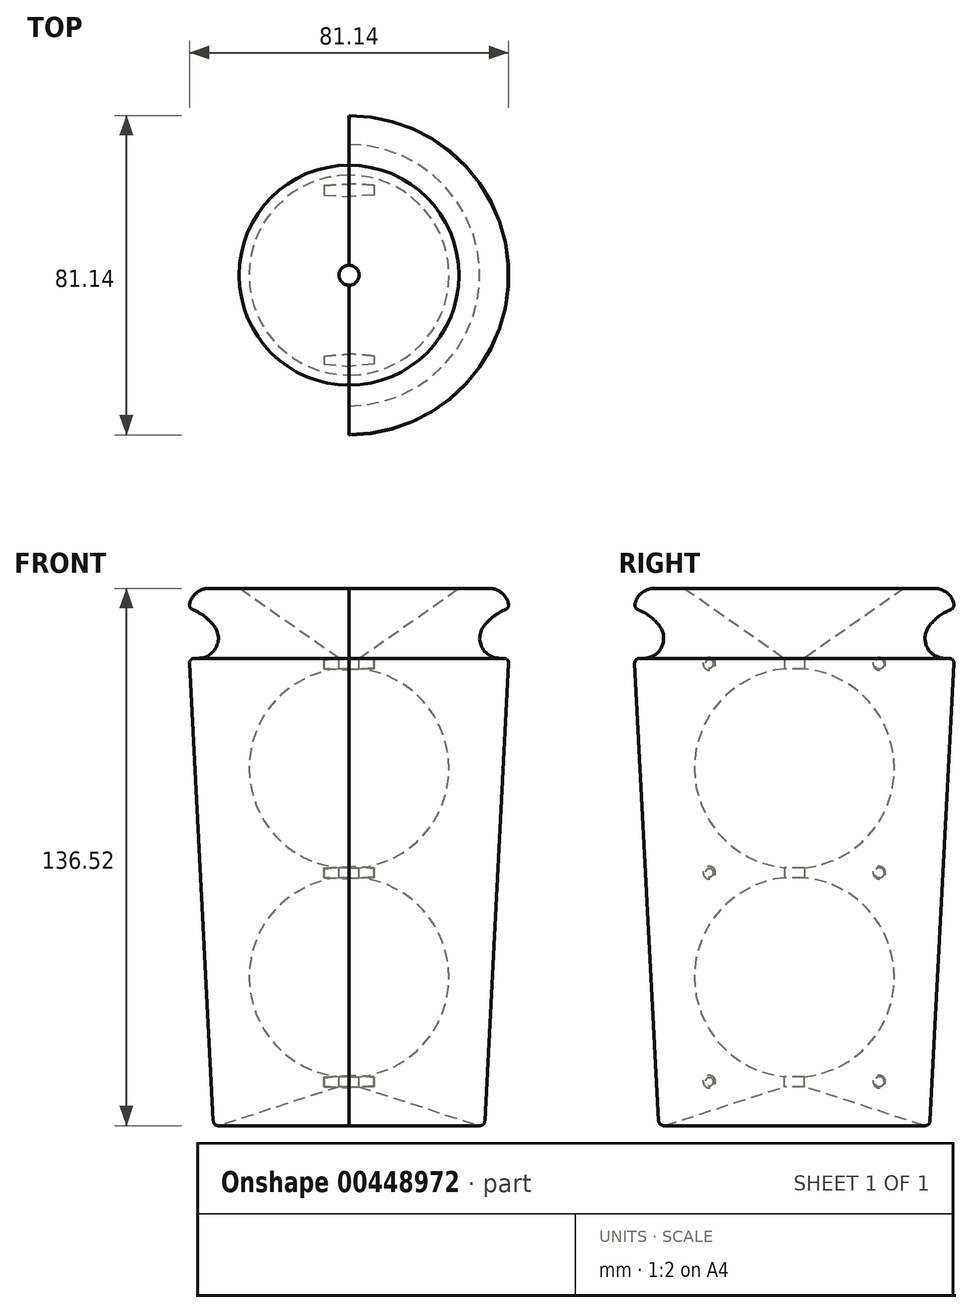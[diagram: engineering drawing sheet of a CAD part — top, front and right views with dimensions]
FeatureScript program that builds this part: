
annotation { "Feature Type Name" : "Feature", "Feature Type Description" : "" }
export const myFeature = defineFeature(function(context is Context, id is Id, definition is map)
    precondition{}
    {
        {
            var Q0;
            Q0=qCreatedBy(makeId("Front.planeOp"),FACE);
            var sketch = newSketch(context, id + "F0", { "sketchPlane" : qUnion([Q0])});
            skLineSegment(sketch, "E0", {"start": v(-40.64, 0) * mm, "end": v(-34.4, -119.19) * mm});
            skLineSegment(sketch, "E1", {"start": v(-40.64, 0) * mm, "end": v(-31.74, 0) * mm});
            skArc(sketch, "E2", {"start": v(-2.54, -2.67) * mm, "mid": v(-25.4, -27.94) * mm, "end": v(-2.54, -53.21) * mm});
            skLineSegment(sketch, "E3", {"start": v(-40.63, 17.78) * mm, "end": v(-27.93, 17.78) * mm});
            skLineSegment(sketch, "E4", {"start": v(-27.93, 17.78) * mm, "end": v(-2.54, 0) * mm});
            skLineSegment(sketch, "E5", {"start": v(-2.54, 0) * mm, "end": v(-2.54, -2.67) * mm});
            skPoint(sketch, "E6", {"position": v(-20.32, 0) * mm});
            skLineSegment(sketch, "E7", {"start": v(-40.63, 17.78) * mm, "end": v(-40.63, 12.7) * mm});
            skArc(sketch, "E8", {"start": v(-31.74, 0) * mm, "mid": v(-34.02, 7.86) * mm, "end": v(-40.63, 12.7) * mm});
            skPoint(sketch, "E9.end.orphan", {"position": v(0, -2.54) * mm});
            skPoint(sketch, "E9.start.orphan", {"position": v(0, 0) * mm});
            skLineSegment(sketch, "E10", {"start": v(-2.54, -53.21) * mm, "end": v(-2.54, -55.75) * mm});
            skArc(sketch, "E11", {"start": v(-2.54, -55.75) * mm, "mid": v(-25.4, -81.03) * mm, "end": v(-2.54, -106.3) * mm});
            skLineSegment(sketch, "E12", {"start": v(-2.54, -108.84) * mm, "end": v(-2.54, -106.3) * mm});
            skLineSegment(sketch, "E13", {"start": v(-2.54, -106.3) * mm, "end": v(-2.54, -55.75) * mm, "construction": true});
            skLineSegment(sketch, "E14", {"start": v(-2.54, -53.21) * mm, "end": v(-2.54, -2.67) * mm, "construction": true});
            skPoint(sketch, "E15.orphan", {"position": v(0, -108.84) * mm});
            skPoint(sketch, "E16.trimOffspring.start.orphan", {"position": v(0, -53.34) * mm});
            skLineSegment(sketch, "E17", {"start": v(0, -2.54) * mm, "end": v(0, -108.84) * mm, "construction": true});
            skLineSegment(sketch, "E18", {"start": v(-34.4, -119.19) * mm, "end": v(-2.54, -108.84) * mm});
            skLineSegment(sketch, "E19", {"start": v(-2.54, -108.84) * mm, "end": v(0, -108.84) * mm, "construction": true});
            skSolve(sketch);
        }
        {
            var Q0;
            Q0 = qSketchRegion(id + "F0", true);
            var Q1;
            Q1=sQuery(id+"F0.wireOp",EDGE,"E17");
            revolve(context, id + "F1", {"entities" : qUnion([Q0]), "axis" : qUnion([Q1]), "revolveType" : RevolveType.SYMMETRIC, "angle" : 180 * degree});
        }
        {
            var Q0;
            Q0=makeQuery(id+"F1.opRevolve","CAP_FACE",FACE,{"disambiguationData":[OSD([sQuery(id+"F0.wireOp",EDGE,"E0"),sQuery(id+"F0.wireOp",EDGE,"E1"),sQuery(id+"F0.wireOp",EDGE,"E2"),sQuery(id+"F0.wireOp",EDGE,"E3"),sQuery(id+"F0.wireOp",EDGE,"E4"),sQuery(id+"F0.wireOp",EDGE,"E5"),sQuery(id+"F0.wireOp",EDGE,"E7"),sQuery(id+"F0.wireOp",EDGE,"E8"),sQuery(id+"F0.wireOp",EDGE,"E10"),sQuery(id+"F0.wireOp",EDGE,"E11"),sQuery(id+"F0.wireOp",EDGE,"E12"),sQuery(id+"F0.wireOp",EDGE,"E18")])],"isStart":true});
            var sketch = newSketch(context, id + "F2", { "sketchPlane" : qUnion([Q0])});
            skLineSegment(sketch, "E20", {"start": v(-21.59, -27.94) * mm, "end": v(0, -27.94) * mm, "construction": true});
            skPoint(sketch, "E21", {"position": v(-25.4, -27.94) * mm});
            skLineSegment(sketch, "E22", {"start": v(0, -81.03) * mm, "end": v(-21.59, -81.03) * mm, "construction": true});
            skPoint(sketch, "E22.endSnap0", {"position": v(-25.4, -81.03) * mm});
            skLineSegment(sketch, "E23", {"start": v(-21.59, -81.03) * mm, "end": v(-21.59, -27.94) * mm, "construction": true});
            skCircle(sketch, "E24", {"center": v(-21.59, -54.48) * mm, "radius": 1.59 * mm});
            skCircle(sketch, "E25.MirrorC", {"center": v(-21.59, -1.4) * mm, "radius": 1.59 * mm});
            skCircle(sketch, "E26.MirrorC", {"center": v(-21.59, -107.57) * mm, "radius": 1.59 * mm});
            skSolve(sketch);
        }
        {
            var Q0;
            Q0 = qSketchRegion(id + "F2", true);
            extrude(context, id + "F3", {"entities" : qUnion([Q0]), "operationType" : NewBodyOperationType.ADD, "depth" : 6.35 * mm, "hasDraft" : true, "draftAngle" : 5 * degree, "draftPullDirection" : true});
        }
        {
            var Q0;
            Q0=makeQuery(id+"F1.opRevolve","CAP_FACE",FACE,{"disambiguationData":[OSD([sQuery(id+"F0.wireOp",EDGE,"E0"),sQuery(id+"F0.wireOp",EDGE,"E1"),sQuery(id+"F0.wireOp",EDGE,"E2"),sQuery(id+"F0.wireOp",EDGE,"E3"),sQuery(id+"F0.wireOp",EDGE,"E4"),sQuery(id+"F0.wireOp",EDGE,"E5"),sQuery(id+"F0.wireOp",EDGE,"E7"),sQuery(id+"F0.wireOp",EDGE,"E8"),sQuery(id+"F0.wireOp",EDGE,"E10"),sQuery(id+"F0.wireOp",EDGE,"E11"),sQuery(id+"F0.wireOp",EDGE,"E12"),sQuery(id+"F0.wireOp",EDGE,"E18")])],"isStart":false});
            var sketch = newSketch(context, id + "F4", { "sketchPlane" : qUnion([Q0])});
            skCircle(sketch, "E27.0", {"center": v(-21.59, -1.4) * mm, "radius": 1.59 * mm, "construction": true});
            skCircle(sketch, "E28.0", {"center": v(-21.59, -54.48) * mm, "radius": 1.59 * mm, "construction": true});
            skCircle(sketch, "E29.0", {"center": v(-21.59, -107.57) * mm, "radius": 1.59 * mm, "construction": true});
            skCircle(sketch, "E30.MirrorC", {"center": v(21.59, -1.4) * mm, "radius": 1.59 * mm, "construction": true});
            skCircle(sketch, "E31.MirrorC", {"center": v(21.59, -54.48) * mm, "radius": 1.59 * mm, "construction": true});
            skCircle(sketch, "E32.MirrorC", {"center": v(21.59, -107.57) * mm, "radius": 1.59 * mm, "construction": true});
            skCircle(sketch, "E33.MirrorC", {"center": v(21.59, -1.4) * mm, "radius": 1.59 * mm});
            skCircle(sketch, "E34.MirrorC", {"center": v(21.59, -54.48) * mm, "radius": 1.59 * mm});
            skCircle(sketch, "E35.MirrorC", {"center": v(21.59, -107.57) * mm, "radius": 1.59 * mm});
            skSolve(sketch);
        }
        {
            var Q0;
            Q0 = qSketchRegion(id + "F4", true);
            extrude(context, id + "F5", {"entities" : qUnion([Q0]), "operationType" : NewBodyOperationType.REMOVE, "oppositeDirection" : true, "depth" : 6.35 * mm, "hasDraft" : true, "draftAngle" : 3 * degree, "draftPullDirection" : true});
        }
        {
            var Q0;
            Q0=makeQuery(id+"F1.opRevolve","SWEPT_EDGE",EDGE,{"disambiguationData":[OSD([sQuery(id+"F0.wireOp",EDGE,"E1"),sQuery(id+"F0.wireOp",EDGE,"E8")])]});
            var Q1;
            Q1=makeQuery(id+"F1.opRevolve","SWEPT_EDGE",EDGE,{"disambiguationData":[OSD([sQuery(id+"F0.wireOp",EDGE,"E3"),sQuery(id+"F0.wireOp",EDGE,"E7")])]});
            fillet(context, id + "F6", {"entities" : qUnion([Q0, Q1]), "radius" : 5.08 * mm, "tangentPropagation" : true, "allowEdgeOverflow" : false});
        }
        {
            var Q0;
            Q0=makeQuery(id+"F6.opFillet","BLEND_EDGE",EDGE,{"blendedFrom":[makeQuery(id+"F1.opRevolve","SWEPT_EDGE",EDGE,{"disambiguationData":[OSD([sQuery(id+"F0.wireOp",EDGE,"E3"),sQuery(id+"F0.wireOp",EDGE,"E7")])]}),makeQuery(id+"F1.opRevolve","SWEPT_FACE",FACE,{"disambiguationData":[OSD([sQuery(id+"F0.wireOp",EDGE,"E8")])]})],"blendedInto":[makeQuery(id+"F1.opRevolve","SWEPT_FACE",FACE,{"disambiguationData":[OSD([sQuery(id+"F0.wireOp",EDGE,"E8")])]})]});
            var Q1;
            Q1=makeQuery(id+"F1.opRevolve","SWEPT_EDGE",EDGE,{"disambiguationData":[OSD([sQuery(id+"F0.wireOp",EDGE,"E0"),sQuery(id+"F0.wireOp",EDGE,"E1")])]});
            var Q2;
            Q2=makeQuery(id+"F1.opRevolve","SWEPT_EDGE",EDGE,{"disambiguationData":[OSD([sQuery(id+"F0.wireOp",EDGE,"E0"),sQuery(id+"F0.wireOp",EDGE,"E18")])]});
            fillet(context, id + "F7", {"entities" : qUnion([Q0, Q1, Q2]), "radius" : 1.27 * mm, "tangentPropagation" : true, "allowEdgeOverflow" : false});
        }
        {
            var Q0;
            Q0=makeQuery(id+"F1.opRevolve","SWEPT_BODY",BODY,{"disambiguationData":[OSD([sQuery(id+"F0.wireOp",EDGE,"E0"),sQuery(id+"F0.wireOp",EDGE,"E1"),sQuery(id+"F0.wireOp",EDGE,"E2"),sQuery(id+"F0.wireOp",EDGE,"E3"),sQuery(id+"F0.wireOp",EDGE,"E4"),sQuery(id+"F0.wireOp",EDGE,"E5"),sQuery(id+"F0.wireOp",EDGE,"E7"),sQuery(id+"F0.wireOp",EDGE,"E8"),sQuery(id+"F0.wireOp",EDGE,"E10"),sQuery(id+"F0.wireOp",EDGE,"E11"),sQuery(id+"F0.wireOp",EDGE,"E12"),sQuery(id+"F0.wireOp",EDGE,"E18")])]});
            var Q1;
            Q1=makeQuery(id+"F1.opRevolve","CAP_FACE",FACE,{"disambiguationData":[OSD([sQuery(id+"F0.wireOp",EDGE,"E0"),sQuery(id+"F0.wireOp",EDGE,"E1"),sQuery(id+"F0.wireOp",EDGE,"E2"),sQuery(id+"F0.wireOp",EDGE,"E3"),sQuery(id+"F0.wireOp",EDGE,"E4"),sQuery(id+"F0.wireOp",EDGE,"E5"),sQuery(id+"F0.wireOp",EDGE,"E7"),sQuery(id+"F0.wireOp",EDGE,"E8"),sQuery(id+"F0.wireOp",EDGE,"E10"),sQuery(id+"F0.wireOp",EDGE,"E11"),sQuery(id+"F0.wireOp",EDGE,"E12"),sQuery(id+"F0.wireOp",EDGE,"E18")])],"isStart":true});
            mirror(context, id + "F8", {"entities" : qUnion([Q0]), "mirrorPlane" : qUnion([Q1])});
        }
    });
